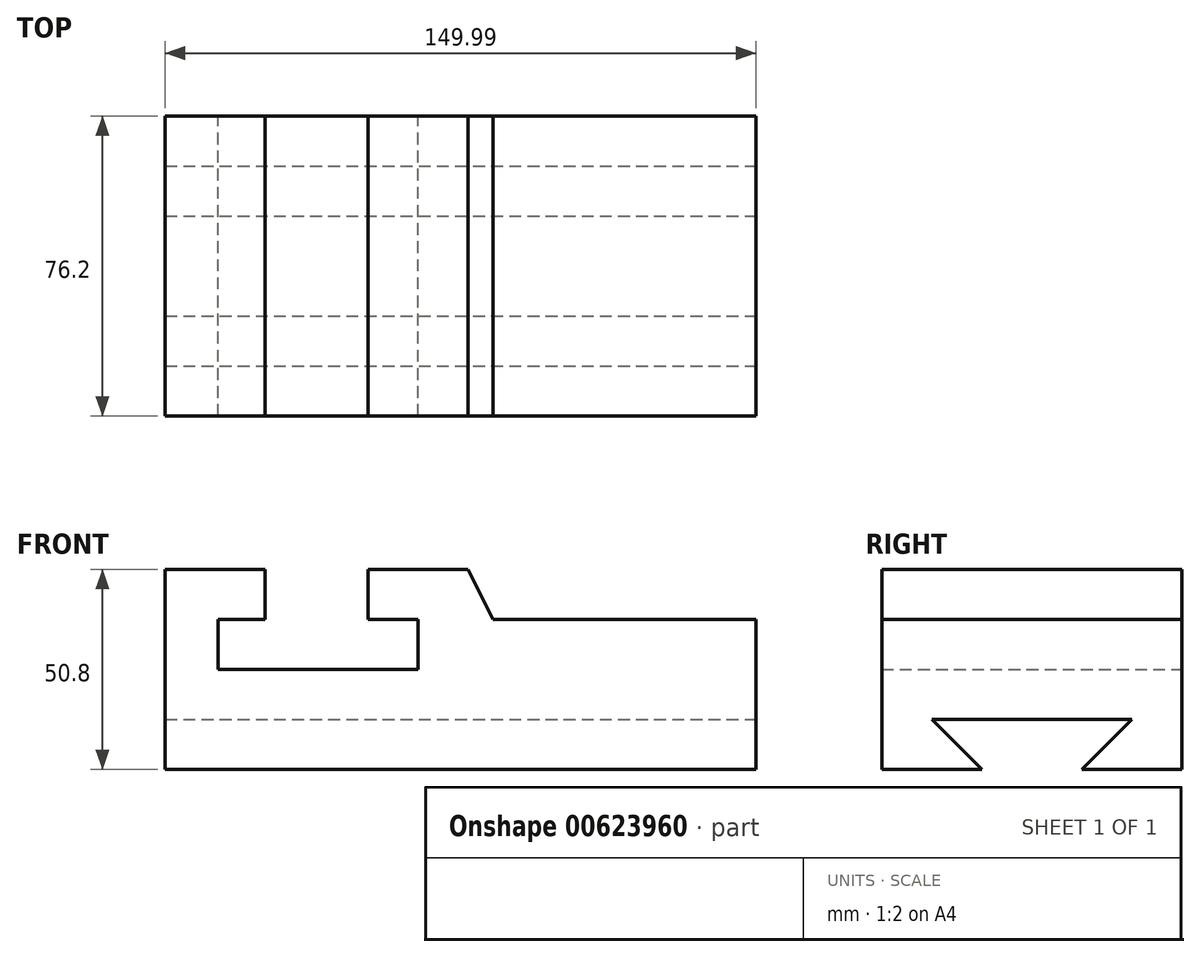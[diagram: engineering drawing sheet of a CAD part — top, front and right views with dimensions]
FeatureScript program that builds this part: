
annotation { "Feature Type Name" : "Feature", "Feature Type Description" : "" }
export const myFeature = defineFeature(function(context is Context, id is Id, definition is map)
    precondition{}
    {
        {
            var Q0;
            Q0=qCreatedBy(makeId("Front.planeOp"),FACE);
            var sketch = newSketch(context, id + "F0", { "sketchPlane" : qUnion([Q0])});
            skLineSegment(sketch, "E0", {"start": v(0, 0) * mm, "end": v(0, 50.8) * mm});
            skLineSegment(sketch, "E1", {"start": v(0, 50.8) * mm, "end": v(25.4, 50.8) * mm});
            skLineSegment(sketch, "E2", {"start": v(25.4, 50.8) * mm, "end": v(25.4, 38.1) * mm});
            skLineSegment(sketch, "E3", {"start": v(25.4, 38.1) * mm, "end": v(13.4, 38.1) * mm});
            skLineSegment(sketch, "E4", {"start": v(13.4, 38.1) * mm, "end": v(13.4, 25.4) * mm});
            skLineSegment(sketch, "E5", {"start": v(13.4, 25.4) * mm, "end": v(64.2, 25.4) * mm});
            skLineSegment(sketch, "E6", {"start": v(64.2, 25.4) * mm, "end": v(64.2, 38.1) * mm});
            skLineSegment(sketch, "E7", {"start": v(64.2, 38.1) * mm, "end": v(51.5, 38.1) * mm});
            skLineSegment(sketch, "E8", {"start": v(51.5, 38.1) * mm, "end": v(51.5, 50.8) * mm});
            skLineSegment(sketch, "E9", {"start": v(51.5, 50.8) * mm, "end": v(76.9, 50.8) * mm});
            skLineSegment(sketch, "E10", {"start": v(-2.41, 0) * mm, "end": v(149.99, 0) * mm});
            skLineSegment(sketch, "E11", {"start": v(149.99, 0) * mm, "end": v(149.99, 38.1) * mm});
            skLineSegment(sketch, "E12", {"start": v(149.99, 38.1) * mm, "end": v(99.19, 38.1) * mm});
            skPoint(sketch, "E13.endSnap0", {"position": v(57.85, 38.1) * mm});
            skLineSegment(sketch, "E14", {"start": v(99.19, 38.1) * mm, "end": v(83.25, 38.1) * mm});
            skLineSegment(sketch, "E15", {"start": v(76.9, 50.8) * mm, "end": v(83.25, 38.1) * mm});
            skSolve(sketch);
        }
        {
            var Q0;
            Q0 = qSketchRegion(id + "F0", true);
            extrude(context, id + "F1", {"entities" : qUnion([Q0]), "depth" : 76.2 * mm, "offsetDistance" : 25.4 * mm});
        }
        {
            var Q0;
            Q0=makeQuery(id+"F1.opExtrude","SWEPT_FACE",FACE,{"disambiguationData":[OSD([sQuery(id+"F0.wireOp",EDGE,"E11")])]});
            var sketch = newSketch(context, id + "F2", { "sketchPlane" : qUnion([Q0])});
            skLineSegment(sketch, "E16", {"start": v(-76.2, 0) * mm, "end": v(-50.8, 0) * mm});
            skLineSegment(sketch, "E17", {"start": v(0, 0) * mm, "end": v(-25.4, 0) * mm});
            skLineSegment(sketch, "E18", {"start": v(-38.1, 12.7) * mm, "end": v(-12.7, 12.7) * mm});
            skLineSegment(sketch, "E19", {"start": v(-38.1, 12.7) * mm, "end": v(-63.5, 12.7) * mm});
            skLineSegment(sketch, "E20", {"start": v(-25.4, 0) * mm, "end": v(-12.7, 12.7) * mm});
            skLineSegment(sketch, "E21", {"start": v(-50.8, 0) * mm, "end": v(-63.5, 12.7) * mm});
            skSolve(sketch);
        }
        {
            var Q0;
            Q0 = qSketchRegion(id + "F2", true);
            var Q1;
            Q1=makeQuery(id+"F2.imprint","IMPRINT",FACE,{"disambiguationData":[TD([[makeQuery(id+"F2.imprint","IMPRINT",EDGE,{"derivedFrom":sQuery(id+"F2.wireOp",EDGE,"E18")}),-1.0]])]});
            extrude(context, id + "F3", {"entities" : qUnion([Q0, Q1]), "operationType" : NewBodyOperationType.REMOVE, "oppositeDirection" : true, "depth" : 195.83 * mm, "offsetDistance" : 25.4 * mm});
        }
    });
